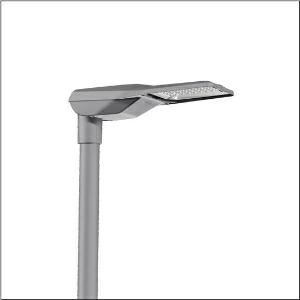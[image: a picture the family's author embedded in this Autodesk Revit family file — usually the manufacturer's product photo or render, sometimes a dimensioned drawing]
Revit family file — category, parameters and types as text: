
# Revit family: streetlight_sl_21_iq_mini___pl52_5xe2h31g08gb_d0f1
name_source: partatom
category: Lighting Fixtures
units: mm (PartAtom-declared; Revit-internal decimal feet)

## family parameters
Cut with Voids When Loaded = No
Host = Face
Light Source = No
Part Type = Normal
Room Calculation Point = No
Round Connector Dimension = Use Diameter
Shared = No

## types (1)
- --- (1 x LED, 5580 lm, 37.1 W, 3000K)
    Apparent Load = 37 VA
    CIE Flux Codes = 27 59 98 100 100
    Color Rendering = 70
    Color Temperature = 3000K
    Default Elevation = 1800 mm
    Description = Streetlight SL 21 iQ mini, mast luminaire, primary light control with lens, of PMMA, primary optical cover: cover, of toughened safety glass, transparent, light distribution: PL52, light emission: direct distribution, primary light characteristic: asymmetric, installation type: post-top, side-entry, LED, High Power LED, rated luminous flux: 5.580lm, luminous efficacy: 150lm/W, light colour: 730, colour temperature: 3000K, control: Street-Remote, Auto-Match, Temp-Guard, Lumen-Switch, Night-Set, Smart-Wire, Light-Fading, Desk-Remote (wireless, voltage-free reading and setting of iQ features in the workshop via application-optimized NFC function/RFID function), optimised constant luminous flux control (CLO 2.0), presetting dimming linear, mains connection: 220..240V, AC, 50/60Hz, start of lifetime: 37W, end of service life: 39W, reduction: 18W, luminaire housing, of diecast aluminium, powder-coated, Siteco® metallic grey (DB 702S), corrosivity category C5 mid according to DIN EN ISO 12944, please order mast flange separately, inclination adjustable: 0°, 5°, 10°, 15°, sealing non-destructively replaceable, multi-level sealing system, length: 628mm, width: 235mm, height: 110mm, mast flange for spigot size: 42mm (side-entry): 5XC10008XM4, 60/48mm (side-entry/post-top): 5XC10108XM2, 76/60mm (side-entry/post-top): 5XC10108XM1, protection rating (complete): IP66, insulation class (complete): insulation class II (safety insulation), certification: CE, ENEC, ENEC+, VDE, impact resistance: IK09, permissible operating ambient temperature for outdoor applications: -40..+50°C, standard-compliant lighting for roads and squares, packaging unit: 1 piece

Light Distribution: PL52
    Height = 110 mm
    Lamp = 1 x LED
    Lamp Light Flux = 5580 lm
    Lamp Power = 37.1 W
    Lamp count = 1
    Length = 625 mm
    Luminous efficacy = 150 lm/W
    Manufacturer = Siteco
    ModVariant = No
    Model = 5XE2H31G08GB
    Number of Poles = 1
    OnlyDefault = Yes
    Power Factor = 1
    Product Name = Streetlight SL 21 iQ mini | PL52
    Product group = mast luminaire | pylon top
    ProductGroupID = 6100
    Protection Class = Protection class II
    Protection Degree = IP 66
    RLX_Detail_Level = 1
    RLX_Emergency_Light_Flux = 0 lm
    RLX_Emergency_Type = 0
    RLX_Emergency_Type_DB = No
    RlxData = <blob elided: 101721 chars, md5=61f55539>
    Socket = socket
    Standby Power = 0 W
    System Light Flux = 5580 lm
    System Power = 37 W
    Type Comments = factory setting: luminous flux: 100 % | dim-lin: 254 | 385 mA
    Type Image = l_1003519.jpg
    URL = http://relux.com
    VarID = @adj_124311
    Voltage = 0 V
    Weight = 0.00 kg
    Width = 234 mm

## geometry (parser evidence)
native form markers: Blend x4, Sweep x12
no freeform markers — native parametric forms only
